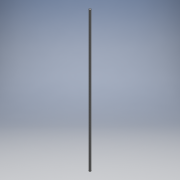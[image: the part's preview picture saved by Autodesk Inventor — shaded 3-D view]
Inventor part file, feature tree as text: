
AUTODESK INVENTOR PART (.ipt)
format: ipt  version: 2018 (Build 220112000, 112)  size: 92,672 bytes
history: native  units: mm
features: extrude x1, thread x1, sketch x1
ambient origin geometry x8: Origin, YZ Plane, XZ Plane, XY Plane, X Axis, Y Axis, Z Axis, Center Point
bodies: Solid1 (feature_tree)
feature tree (3):
  extrude  "Extrusion1"  Depth=422.0mm TaperAngle=0.0deg
  thread  "Thread1"  [1 undecoded]
  sketch  "Sketch1"  dims[d0=6.0mm d1=422.0mm d2=0.0mm d3=10.0mm d4=0.0mm]
note: 1 required parameter value undecoded (feature->parameter linkage not recoverable at this tier; creation-order binding heuristic only, values carry confidence <= 0.55)
